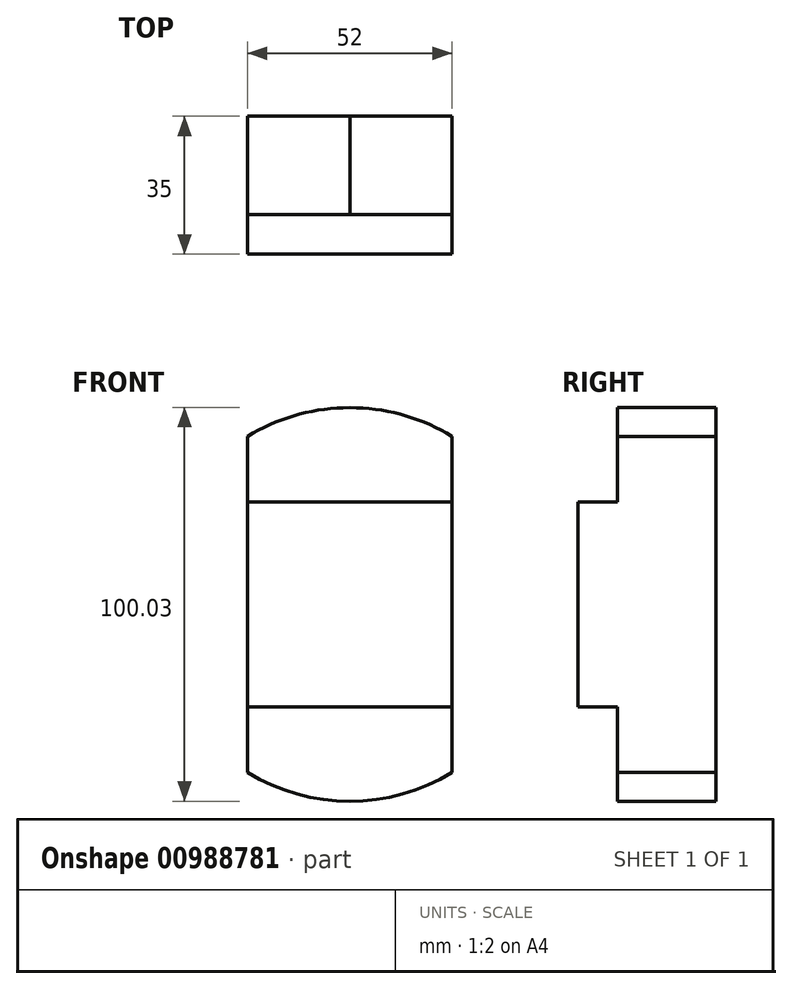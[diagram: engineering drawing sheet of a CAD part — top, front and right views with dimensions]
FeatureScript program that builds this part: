
annotation { "Feature Type Name" : "Feature", "Feature Type Description" : "" }
export const myFeature = defineFeature(function(context is Context, id is Id, definition is map)
    precondition{}
    {
        {
            var Q0;
            Q0=qCreatedBy(makeId("Front.planeOp"),FACE);
            var sketch = newSketch(context, id + "F0", { "sketchPlane" : qUnion([Q0])});
            skCircle(sketch, "E0", {"center": v(0, 0) * mm, "radius": 26 * mm});
            skArc(sketch, "E1", {"start": v(-26, -42.7) * mm, "mid": v(0, -50) * mm, "end": v(26, -42.7) * mm});
            skLineSegment(sketch, "E2", {"start": v(-26, 0) * mm, "end": v(-26, -42.7) * mm});
            skLineSegment(sketch, "E3", {"start": v(26, 0) * mm, "end": v(26, -42.7) * mm});
            skLineSegment(sketch, "E4", {"start": v(-26, 0) * mm, "end": v(-26, 42.7) * mm});
            skLineSegment(sketch, "E5", {"start": v(-1.67, 49.97) * mm, "end": v(0, 50.03) * mm});
            skLineSegment(sketch, "E6", {"start": v(0, 50.03) * mm, "end": v(1.67, 49.97) * mm});
            skLineSegment(sketch, "E7", {"start": v(26, 42.7) * mm, "end": v(26, 0) * mm});
            skLineSegment(sketch, "E8.bottom", {"start": v(26, -26) * mm, "end": v(-26, -26) * mm});
            skLineSegment(sketch, "E8.top", {"start": v(26, 26) * mm, "end": v(-26, 26) * mm});
            skLineSegment(sketch, "E8.left", {"start": v(26, -26) * mm, "end": v(26, 26) * mm});
            skLineSegment(sketch, "E8.right", {"start": v(-26, -26) * mm, "end": v(-26, 26) * mm});
            skPoint(sketch, "E8.cornerSnap0", {"position": v(26, -26) * mm});
            skCircle(sketch, "E9", {"center": v(0, 0) * mm, "radius": 12.7 * mm});
            skArc(sketch, "E10.trimOffspring", {"start": v(26, 42.7) * mm, "mid": v(14.3, 47.91) * mm, "end": v(1.67, 49.97) * mm});
            skPoint(sketch, "E11.orphan", {"position": v(26, -52) * mm});
            skPoint(sketch, "E12.end.orphan", {"position": v(0, -50.03) * mm});
            skPoint(sketch, "E13.orphan", {"position": v(26, 49.16) * mm});
            skArc(sketch, "E14.trimOffspring", {"start": v(-1.67, 49.97) * mm, "mid": v(-14.3, 47.91) * mm, "end": v(-26, 42.7) * mm});
            skSolve(sketch);
        }
        {
            var Q0;
            {var subQ0=sQuery(id+"F0.wireOp",EDGE,"E8.right");var subQ1=sQuery(id+"F0.wireOp",EDGE,"E0");var subQ2=makeQuery(id+"F0.imprint","INTERSECT",VERTEX,{"derivedFrom":[subQ1,subQ0]});Q0=makeQuery(id+"F0.imprint","IMPRINT",FACE,{"disambiguationData":[TD([[makeQuery(id+"F0.imprint","IMPRINT",EDGE,{"disambiguationData":[TD([[subQ2,1.0]])],"derivedFrom":subQ1}),-1.0]])]});}
            var Q1;
            {var subQ0=sQuery(id+"F0.wireOp",EDGE,"E8.left");var subQ1=sQuery(id+"F0.wireOp",EDGE,"E0");var subQ2=makeQuery(id+"F0.imprint","INTERSECT",VERTEX,{"derivedFrom":[subQ1,subQ0]});Q1=makeQuery(id+"F0.imprint","IMPRINT",FACE,{"disambiguationData":[TD([[makeQuery(id+"F0.imprint","IMPRINT",EDGE,{"disambiguationData":[TD([[subQ2,-1.0]])],"derivedFrom":subQ1}),-1.0]])]});}
            var Q2;
            {var subQ0=sQuery(id+"F0.wireOp",EDGE,"E8.right");var subQ1=sQuery(id+"F0.wireOp",EDGE,"E0");var subQ2=makeQuery(id+"F0.imprint","INTERSECT",VERTEX,{"derivedFrom":[subQ1,subQ0]});Q2=makeQuery(id+"F0.imprint","IMPRINT",FACE,{"disambiguationData":[TD([[makeQuery(id+"F0.imprint","IMPRINT",EDGE,{"disambiguationData":[TD([[subQ2,-1.0]])],"derivedFrom":subQ1}),-1.0]])]});}
            var Q3;
            {var subQ0=sQuery(id+"F0.wireOp",EDGE,"E8.left");var subQ1=sQuery(id+"F0.wireOp",EDGE,"E0");var subQ2=makeQuery(id+"F0.imprint","INTERSECT",VERTEX,{"derivedFrom":[subQ1,subQ0]});Q3=makeQuery(id+"F0.imprint","IMPRINT",FACE,{"disambiguationData":[TD([[makeQuery(id+"F0.imprint","IMPRINT",EDGE,{"disambiguationData":[TD([[subQ2,1.0]])],"derivedFrom":subQ1}),-1.0]])]});}
            var Q4;
            Q4=makeQuery(id+"F0.imprint","IMPRINT",FACE,{"disambiguationData":[TD([[makeQuery(id+"F0.imprint","IMPRINT",EDGE,{"derivedFrom":sQuery(id+"F0.wireOp",EDGE,"E9")}),-1.0]])]});
            var Q5;
            Q5=makeQuery(id+"F0.imprint","IMPRINT",FACE,{"disambiguationData":[TD([[makeQuery(id+"F0.imprint","IMPRINT",EDGE,{"derivedFrom":sQuery(id+"F0.wireOp",EDGE,"E9")}),1.0]])]});
            extrude(context, id + "F1", {"entities" : qUnion([Q0, Q1, Q2, Q3, Q4, Q5]), "depth" : 10 * mm, "offsetDistance" : 25 * mm});
        }
        {
            var Q0;
            Q0 = qSketchRegion(id + "F0", true);
            var Q1;
            Q1=makeQuery(id+"F1.opExtrude","CAP_FACE",FACE,{"disambiguationData":[OSD([sQuery(id+"F0.wireOp",EDGE,"E8.bottom"),sQuery(id+"F0.wireOp",EDGE,"E8.top"),sQuery(id+"F0.wireOp",EDGE,"E8.left"),sQuery(id+"F0.wireOp",EDGE,"E8.right")])],"isStart":false});
            extrude(context, id + "F2", {"entities" : qUnion([Q0, Q1]), "operationType" : NewBodyOperationType.ADD, "depth" : 25 * mm, "offsetDistance" : 25 * mm});
        }
    });
